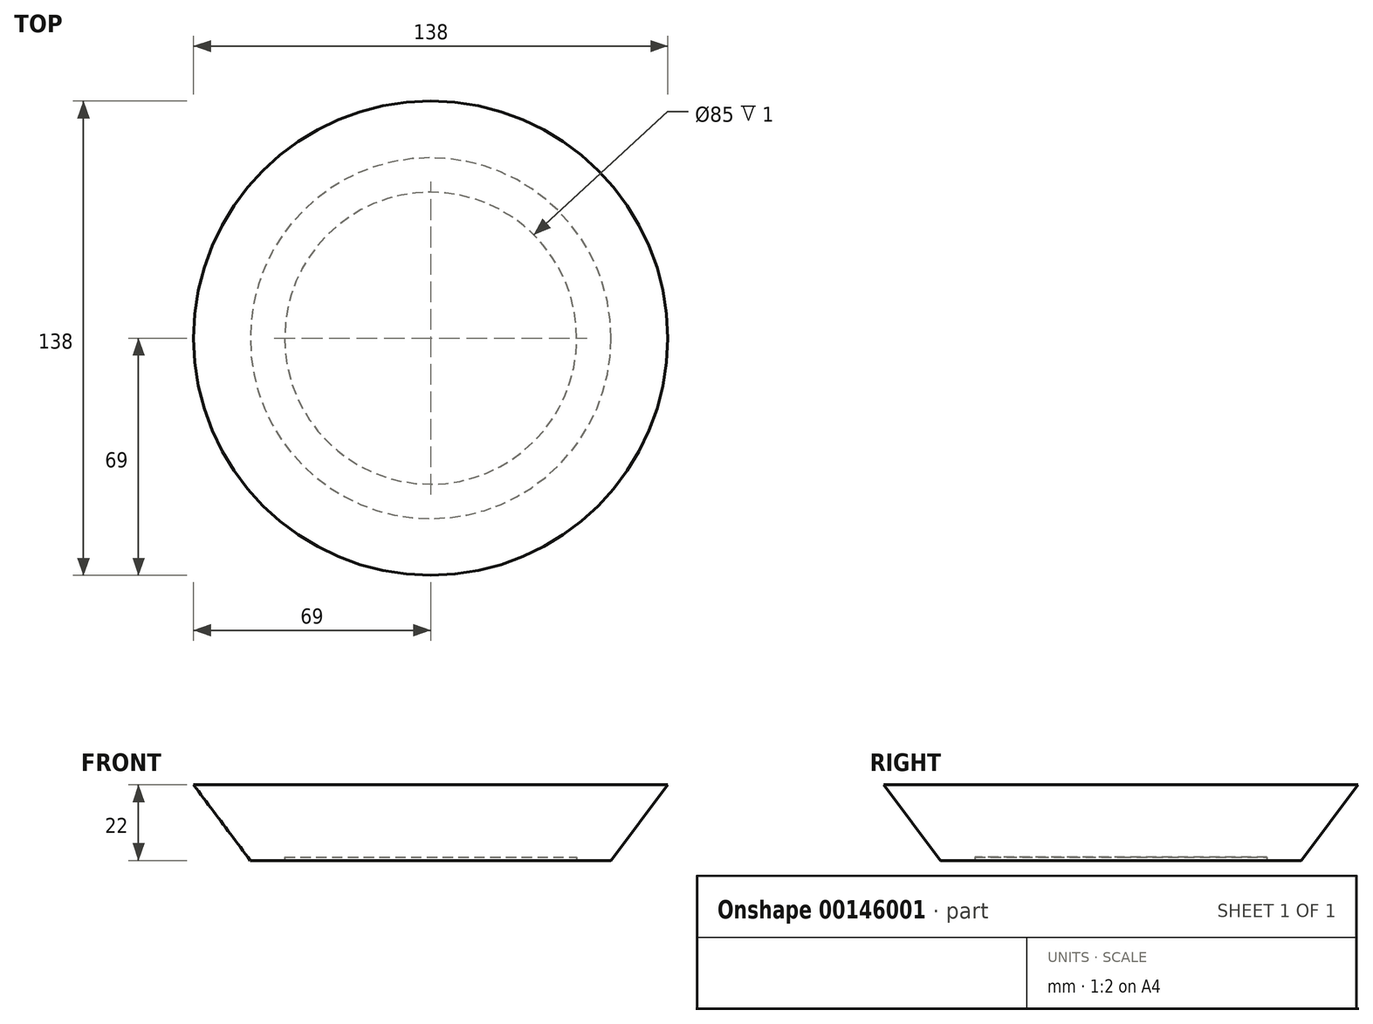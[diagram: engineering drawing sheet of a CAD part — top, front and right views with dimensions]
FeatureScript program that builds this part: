
annotation { "Feature Type Name" : "Feature", "Feature Type Description" : "" }
export const myFeature = defineFeature(function(context is Context, id is Id, definition is map)
    precondition{}
    {
        {
            var Q0;
            Q0=qCreatedBy(makeId("Front.planeOp"),FACE);
            var sketch = newSketch(context, id + "F0", { "sketchPlane" : qUnion([Q0])});
            skLineSegment(sketch, "E0", {"start": v(0, 1) * mm, "end": v(42.5, 1) * mm});
            skLineSegment(sketch, "E1", {"start": v(42.5, 1) * mm, "end": v(42.5, 0) * mm});
            skLineSegment(sketch, "E2", {"start": v(42.5, 0) * mm, "end": v(52.5, 0) * mm});
            skLineSegment(sketch, "E3", {"start": v(0, 1) * mm, "end": v(0, 22) * mm});
            skLineSegment(sketch, "E4", {"start": v(0, 22) * mm, "end": v(69, 22) * mm});
            skLineSegment(sketch, "E5", {"start": v(69, 22) * mm, "end": v(52.5, 0) * mm});
            skSolve(sketch);
        }
        {
            var Q0;
            Q0=makeQuery(id+"F0.imprint","IMPRINT",FACE,{"disambiguationData":[TD([[makeQuery(id+"F0.imprint","IMPRINT",EDGE,{"derivedFrom":sQuery(id+"F0.wireOp",EDGE,"E0")}),1.0]])]});
            var Q1;
            Q1=sQuery(id+"F0.wireOp",EDGE,"E3");
            revolve(context, id + "F1", {"entities" : qUnion([Q0]), "axis" : qUnion([Q1]), "revolveType" : RevolveType.FULL});
        }
    });
